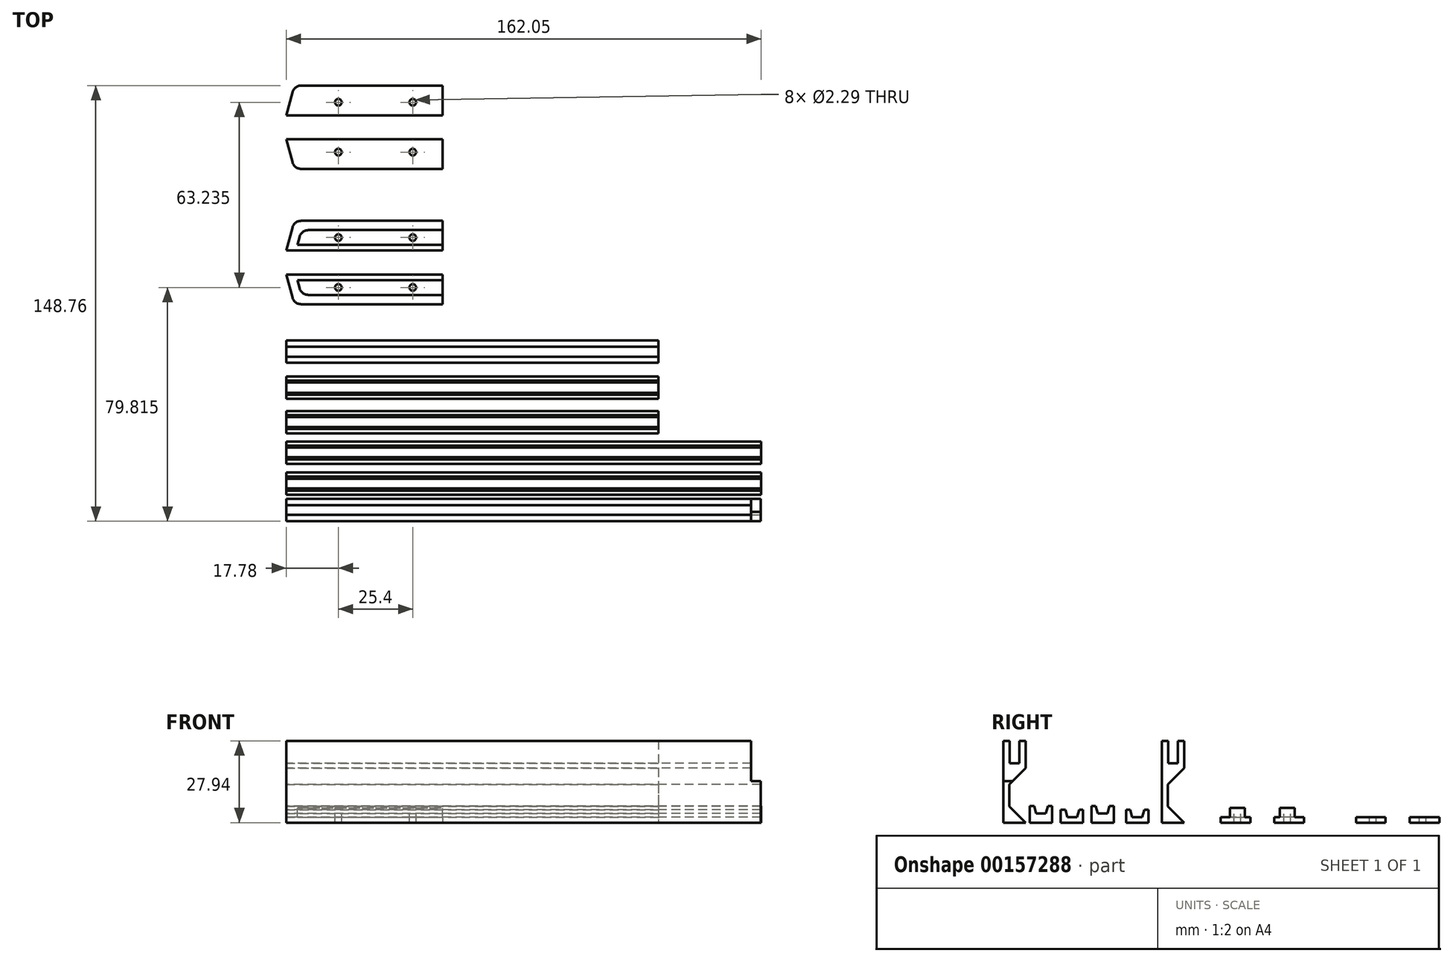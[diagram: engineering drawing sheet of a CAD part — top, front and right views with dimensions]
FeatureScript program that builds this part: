
annotation { "Feature Type Name" : "Feature", "Feature Type Description" : "" }
export const myFeature = defineFeature(function(context is Context, id is Id, definition is map)
    precondition{}
    {
        {
            var Q0;
            Q0=qCreatedBy(makeId("Top.planeOp"),FACE);
            var sketch = newSketch(context, id + "F0", { "sketchPlane" : qUnion([Q0])});
            skLineSegment(sketch, "E0", {"start": v(5.06, 0) * mm, "end": v(53.34, 0) * mm});
            skLineSegment(sketch, "E1", {"start": v(0, 10.16) * mm, "end": v(53.34, 10.16) * mm});
            skLineSegment(sketch, "E2", {"start": v(53.34, 10.16) * mm, "end": v(53.34, 0) * mm});
            skPoint(sketch, "E3.visualSharp", {"position": v(0, 0) * mm});
            skLineSegment(sketch, "E4", {"start": v(0, 14.23) * mm, "end": v(64.91, 14.23) * mm, "construction": true});
            skLineSegment(sketch, "E5", {"start": v(2.12, 2.26) * mm, "end": v(0, 10.16) * mm});
            skPoint(sketch, "E6.visualSharp", {"position": v(2.72, 0) * mm});
            skArc(sketch, "E6.filletArc", {"start": v(2.12, 2.26) * mm, "mid": v(3.2, 0.63) * mm, "end": v(5.06, 0) * mm});
            skLineSegment(sketch, "E7.MirrorCS", {"start": v(0, 18.3) * mm, "end": v(53.34, 18.3) * mm});
            skLineSegment(sketch, "E8.MirrorCS", {"start": v(2.12, 26.2) * mm, "end": v(0, 18.3) * mm});
            skArc(sketch, "E9.MirrorCS", {"start": v(2.12, 26.2) * mm, "mid": v(3.2, 27.83) * mm, "end": v(5.06, 28.46) * mm});
            skLineSegment(sketch, "E10.MirrorCS", {"start": v(5.06, 28.46) * mm, "end": v(53.34, 28.46) * mm});
            skLineSegment(sketch, "E11.MirrorCS", {"start": v(53.34, 18.3) * mm, "end": v(53.34, 28.46) * mm});
            skLineSegment(sketch, "E12", {"start": v(0, 37.33) * mm, "end": v(59.62, 37.33) * mm, "construction": true});
            skLineSegment(sketch, "E13.MirrorCS", {"start": v(5.06, 46.2) * mm, "end": v(53.34, 46.2) * mm});
            skArc(sketch, "E14.MirrorCS", {"start": v(2.12, 48.46) * mm, "mid": v(3.2, 46.83) * mm, "end": v(5.06, 46.2) * mm});
            skLineSegment(sketch, "E15.MirrorCS", {"start": v(2.12, 48.46) * mm, "end": v(0, 56.36) * mm});
            skLineSegment(sketch, "E16.MirrorCS", {"start": v(0, 56.36) * mm, "end": v(53.34, 56.36) * mm});
            skLineSegment(sketch, "E17.MirrorCS", {"start": v(53.34, 56.36) * mm, "end": v(53.34, 46.2) * mm});
            skLineSegment(sketch, "E18.MirrorCS", {"start": v(0, 64.5) * mm, "end": v(53.34, 64.5) * mm});
            skLineSegment(sketch, "E19.MirrorCS", {"start": v(2.12, 72.4) * mm, "end": v(0, 64.5) * mm});
            skArc(sketch, "E20.MirrorCS", {"start": v(2.12, 72.4) * mm, "mid": v(3.2, 74.04) * mm, "end": v(5.06, 74.66) * mm});
            skLineSegment(sketch, "E21.MirrorCS", {"start": v(5.06, 74.66) * mm, "end": v(53.34, 74.66) * mm});
            skLineSegment(sketch, "E22.MirrorCS", {"start": v(53.34, 64.5) * mm, "end": v(53.34, 74.66) * mm});
            skSolve(sketch);
        }
        {
            var Q0;
            Q0 = qSketchRegion(id + "F0", true);
            extrude(context, id + "F1", {"entities" : qUnion([Q0]), "depth" : 1.9 * mm});
        }
        {
            var Q0;
            Q0=makeQuery(id+"F1.opExtrude","CAP_FACE",FACE,{"disambiguationData":[OSD([sQuery(id+"F0.wireOp",EDGE,"E0"),sQuery(id+"F0.wireOp",EDGE,"E1"),sQuery(id+"F0.wireOp",EDGE,"E2"),sQuery(id+"F0.wireOp",EDGE,"5697KqRH-eI2E-rnLH-nUeZ-s4URGK5m77xj"),sQuery(id+"F0.wireOp",EDGE,"92a76409-ad34-472e-83c1-3b65e62bf029.filletArc")])],"isStart":false});
            var sketch = newSketch(context, id + "F2", { "sketchPlane" : qUnion([Q0])});
            skLineSegment(sketch, "E23", {"start": v(53.34, 10.16) * mm, "end": v(3.3, 10.16) * mm});
            skLineSegment(sketch, "E24", {"start": v(7.5, 3.18) * mm, "end": v(53.34, 3.18) * mm});
            skLineSegment(sketch, "E25", {"start": v(4.57, 5.43) * mm, "end": v(3.3, 10.16) * mm});
            skPoint(sketch, "E26.visualSharp", {"position": v(5.17, 3.18) * mm});
            skArc(sketch, "E26.filletArc", {"start": v(4.57, 5.43) * mm, "mid": v(5.65, 3.8) * mm, "end": v(7.5, 3.18) * mm});
            skLineSegment(sketch, "E27", {"start": v(53.34, 10.16) * mm, "end": v(53.34, 3.18) * mm});
            skLineSegment(sketch, "E28.MirrorCS", {"start": v(53.34, 18.3) * mm, "end": v(3.3, 18.3) * mm});
            skLineSegment(sketch, "E29.MirrorCS", {"start": v(4.57, 23.03) * mm, "end": v(3.3, 18.3) * mm});
            skArc(sketch, "E30.MirrorCS", {"start": v(4.57, 23.03) * mm, "mid": v(5.65, 24.66) * mm, "end": v(7.5, 25.29) * mm});
            skLineSegment(sketch, "E31.MirrorCS", {"start": v(7.5, 25.29) * mm, "end": v(53.34, 25.29) * mm});
            skLineSegment(sketch, "E32.MirrorCS", {"start": v(53.34, 18.3) * mm, "end": v(53.34, 25.29) * mm});
            skSolve(sketch);
        }
        {
            var Q0;
            Q0 = qSketchRegion(id + "F2", true);
            extrude(context, id + "F3", {"entities" : qUnion([Q0]), "operationType" : NewBodyOperationType.ADD, "depth" : 3.15 * mm});
        }
        {
            var Q0;
            Q0=makeQuery(id+"F3.boolean.opBoolean","MERGE",FACE,{"derivedFrom":[makeQuery(id+"F1.opExtrude","SWEPT_FACE",FACE,{"disambiguationData":[OSD([sQuery(id+"F0.wireOp",EDGE,"E2")])]}),makeQuery(id+"F3.opExtrude","SWEPT_FACE",FACE,{"disambiguationData":[OSD([sQuery(id+"F2.wireOp",EDGE,"E27")])]})]});
            var sketch = newSketch(context, id + "F4", { "sketchPlane" : qUnion([Q0])});
            skLineSegment(sketch, "E33", {"start": v(10.16, 1.9) * mm, "end": v(8.26, 1.9) * mm});
            skLineSegment(sketch, "E34", {"start": v(8.26, 1.9) * mm, "end": v(8.26, 5.05) * mm});
            skLineSegment(sketch, "E35", {"start": v(8.26, 5.05) * mm, "end": v(10.16, 5.05) * mm});
            skLineSegment(sketch, "E36", {"start": v(10.16, 5.05) * mm, "end": v(10.16, 1.9) * mm});
            skLineSegment(sketch, "E37", {"start": v(14.23, 0) * mm, "end": v(14.23, 7.96) * mm, "construction": true});
            skLineSegment(sketch, "E38.MirrorCS", {"start": v(18.3, 5.05) * mm, "end": v(18.3, 1.9) * mm});
            skLineSegment(sketch, "E39.MirrorCS", {"start": v(20.2, 5.05) * mm, "end": v(18.3, 5.05) * mm});
            skLineSegment(sketch, "E40.MirrorCS", {"start": v(20.2, 1.9) * mm, "end": v(20.2, 5.05) * mm});
            skLineSegment(sketch, "E41.MirrorCS", {"start": v(18.3, 1.9) * mm, "end": v(20.2, 1.9) * mm});
            skSolve(sketch);
        }
        {
            var Q0;
            Q0 = qSketchRegion(id + "F4", true);
            extrude(context, id + "F5", {"entities" : qUnion([Q0]), "operationType" : NewBodyOperationType.REMOVE, "endBound" : BoundingType.UP_TO_NEXT, "oppositeDirection" : true, "depth" : 25.4 * mm});
        }
        {
            var Q0;
            Q0=makeQuery(id+"F3.opExtrude","CAP_FACE",FACE,{"disambiguationData":[OSD([sQuery(id+"F2.wireOp",EDGE,"E23"),sQuery(id+"F2.wireOp",EDGE,"E24"),sQuery(id+"F2.wireOp",EDGE,"E25"),sQuery(id+"F2.wireOp",EDGE,"E26.filletArc"),sQuery(id+"F2.wireOp",EDGE,"E27")])],"isStart":false});
            var sketch = newSketch(context, id + "F6", { "sketchPlane" : qUnion([Q0])});
            skCircle(sketch, "E42", {"center": v(17.78, 5.72) * mm, "radius": 1.14 * mm});
            skCircle(sketch, "E43", {"center": v(43.18, 5.72) * mm, "radius": 1.14 * mm});
            skCircle(sketch, "E44.MirrorC", {"center": v(17.78, 22.75) * mm, "radius": 1.14 * mm});
            skCircle(sketch, "E45.MirrorC", {"center": v(43.18, 22.75) * mm, "radius": 1.14 * mm});
            skCircle(sketch, "E46.MirrorC", {"center": v(17.78, 51.92) * mm, "radius": 1.14 * mm});
            skCircle(sketch, "E47.MirrorC", {"center": v(43.18, 51.92) * mm, "radius": 1.14 * mm});
            skCircle(sketch, "E48.MirrorC", {"center": v(43.18, 68.95) * mm, "radius": 1.14 * mm});
            skCircle(sketch, "E49.MirrorC", {"center": v(17.78, 68.95) * mm, "radius": 1.14 * mm});
            skSolve(sketch);
        }
        {
            var Q0;
            Q0 = qSketchRegion(id + "F6", true);
            extrude(context, id + "F7", {"entities" : qUnion([Q0]), "operationType" : NewBodyOperationType.REMOVE, "endBound" : BoundingType.THROUGH_ALL, "oppositeDirection" : true, "depth" : 25.4 * mm});
        }
        {
            var Q0;
            Q0=qCreatedBy(makeId("Top.planeOp"),FACE);
            var sketch = newSketch(context, id + "F8", { "sketchPlane" : qUnion([Q0])});
            skLineSegment(sketch, "E50.bottom", {"start": v(0, -12.41) * mm, "end": v(127, -12.41) * mm});
            skLineSegment(sketch, "E50.top", {"start": v(0, -20.03) * mm, "end": v(127, -20.03) * mm});
            skLineSegment(sketch, "E50.left", {"start": v(0, -12.41) * mm, "end": v(0, -20.03) * mm});
            skLineSegment(sketch, "E50.right", {"start": v(127, -12.41) * mm, "end": v(127, -20.03) * mm});
            skSolve(sketch);
        }
        {
            var Q0;
            Q0 = qSketchRegion(id + "F8", true);
            extrude(context, id + "F9", {"entities" : qUnion([Q0]), "depth" : 27.94 * mm});
        }
        {
            var Q0;
            Q0=makeQuery(id+"F9.opExtrude","SWEPT_FACE",FACE,{"disambiguationData":[OSD([sQuery(id+"F8.wireOp",EDGE,"E50.right")])]});
            var sketch = newSketch(context, id + "F10", { "sketchPlane" : qUnion([Q0])});
            skLineSegment(sketch, "E51.bottom", {"start": v(-17.9, 27.94) * mm, "end": v(-14.55, 27.94) * mm});
            skLineSegment(sketch, "E51.top", {"start": v(-17.9, 20.32) * mm, "end": v(-14.55, 20.32) * mm});
            skLineSegment(sketch, "E51.left", {"start": v(-17.9, 27.94) * mm, "end": v(-17.9, 20.32) * mm});
            skLineSegment(sketch, "E51.right", {"start": v(-14.55, 27.94) * mm, "end": v(-14.55, 20.32) * mm});
            skLineSegment(sketch, "E52", {"start": v(-12.41, 18.63) * mm, "end": v(-18, 13.05) * mm});
            skLineSegment(sketch, "E53", {"start": v(-18, 13.05) * mm, "end": v(-18, 5.59) * mm});
            skLineSegment(sketch, "E54", {"start": v(-18, 5.59) * mm, "end": v(-12.41, 0) * mm});
            skLineSegment(sketch, "E55", {"start": v(-12.41, 0) * mm, "end": v(-12.41, 18.63) * mm});
            skSolve(sketch);
        }
        {
            var Q0;
            Q0 = qSketchRegion(id + "F10", true);
            extrude(context, id + "F11", {"entities" : qUnion([Q0]), "operationType" : NewBodyOperationType.REMOVE, "endBound" : BoundingType.UP_TO_NEXT, "oppositeDirection" : true, "depth" : 25.4 * mm});
        }
        {
            var Q0;
            Q0=qCreatedBy(makeId("Top.planeOp"),FACE);
            var sketch = newSketch(context, id + "F12", { "sketchPlane" : qUnion([Q0])});
            skLineSegment(sketch, "E56.bottom", {"start": v(0, -24.66) * mm, "end": v(127, -24.66) * mm});
            skLineSegment(sketch, "E56.top", {"start": v(0, -32.28) * mm, "end": v(127, -32.28) * mm});
            skLineSegment(sketch, "E56.left", {"start": v(0, -24.66) * mm, "end": v(0, -32.28) * mm});
            skLineSegment(sketch, "E56.right", {"start": v(127, -24.66) * mm, "end": v(127, -32.28) * mm});
            skSolve(sketch);
        }
        {
            var Q0;
            Q0 = qSketchRegion(id + "F12", true);
            extrude(context, id + "F13", {"entities" : qUnion([Q0]), "depth" : 4.44 * mm});
        }
        {
            var Q0;
            Q0=makeQuery(id+"F13.opExtrude","SWEPT_FACE",FACE,{"disambiguationData":[OSD([sQuery(id+"F12.wireOp",EDGE,"E56.right")])]});
            var sketch = newSketch(context, id + "F14", { "sketchPlane" : qUnion([Q0])});
            skLineSegment(sketch, "E57", {"start": v(-30.88, 4.45) * mm, "end": v(-30.25, 1.9) * mm});
            skLineSegment(sketch, "E58", {"start": v(-30.25, 1.9) * mm, "end": v(-26.7, 1.9) * mm});
            skLineSegment(sketch, "E59", {"start": v(-26.7, 1.9) * mm, "end": v(-26.06, 4.45) * mm});
            skLineSegment(sketch, "E60", {"start": v(-26.06, 4.45) * mm, "end": v(-30.88, 4.45) * mm});
            skSolve(sketch);
        }
        {
            var Q0;
            Q0 = qSketchRegion(id + "F14", true);
            extrude(context, id + "F15", {"entities" : qUnion([Q0]), "operationType" : NewBodyOperationType.REMOVE, "endBound" : BoundingType.UP_TO_NEXT, "oppositeDirection" : true, "depth" : 25.4 * mm});
        }
        {
            var Q0;
            Q0=qCreatedBy(makeId("Top.planeOp"),FACE);
            var sketch = newSketch(context, id + "F16", { "sketchPlane" : qUnion([Q0])});
            skLineSegment(sketch, "E61.bottom", {"start": v(0, -36.46) * mm, "end": v(127, -36.46) * mm});
            skLineSegment(sketch, "E61.top", {"start": v(0, -44.08) * mm, "end": v(127, -44.08) * mm});
            skLineSegment(sketch, "E61.left", {"start": v(0, -36.46) * mm, "end": v(0, -44.08) * mm});
            skLineSegment(sketch, "E61.right", {"start": v(127, -36.46) * mm, "end": v(127, -44.08) * mm});
            skSolve(sketch);
        }
        {
            var Q0;
            Q0 = qSketchRegion(id + "F16", true);
            extrude(context, id + "F17", {"entities" : qUnion([Q0]), "depth" : 5.7 * mm});
        }
        {
            var Q0;
            Q0=makeQuery(id+"F17.opExtrude","SWEPT_FACE",FACE,{"disambiguationData":[OSD([sQuery(id+"F16.wireOp",EDGE,"E61.right")])]});
            var sketch = newSketch(context, id + "F18", { "sketchPlane" : qUnion([Q0])});
            skLineSegment(sketch, "E62", {"start": v(-42.6, 5.72) * mm, "end": v(-41.92, 3.17) * mm});
            skLineSegment(sketch, "E63", {"start": v(-41.92, 3.17) * mm, "end": v(-38.57, 3.18) * mm});
            skLineSegment(sketch, "E64", {"start": v(-38.57, 3.17) * mm, "end": v(-37.9, 5.72) * mm});
            skLineSegment(sketch, "E65", {"start": v(-42.6, 5.72) * mm, "end": v(-37.9, 5.72) * mm});
            skSolve(sketch);
        }
        {
            var Q0;
            Q0 = qSketchRegion(id + "F18", true);
            extrude(context, id + "F19", {"entities" : qUnion([Q0]), "operationType" : NewBodyOperationType.REMOVE, "endBound" : BoundingType.UP_TO_NEXT, "oppositeDirection" : true, "depth" : 25.4 * mm});
        }
        {
            var Q0;
            Q0=qCreatedBy(makeId("Right.planeOp"),FACE);
            var sketch = newSketch(context, id + "F20", { "sketchPlane" : qUnion([Q0])});
            skLineSegment(sketch, "E66", {"start": v(-66.48, 27.94) * mm, "end": v(-66.48, 18.63) * mm});
            skLineSegment(sketch, "E67", {"start": v(-66.48, 0) * mm, "end": v(-74.1, 0) * mm});
            skLineSegment(sketch, "E68", {"start": v(-74.1, 0) * mm, "end": v(-74.1, 27.94) * mm});
            skLineSegment(sketch, "E69", {"start": v(-74.1, 27.94) * mm, "end": v(-71.96, 27.94) * mm});
            skLineSegment(sketch, "E70.top", {"start": v(-71.96, 20.32) * mm, "end": v(-68.6, 20.32) * mm});
            skLineSegment(sketch, "E70.left", {"start": v(-71.96, 27.94) * mm, "end": v(-71.96, 20.32) * mm});
            skLineSegment(sketch, "E70.right", {"start": v(-68.6, 27.94) * mm, "end": v(-68.6, 20.32) * mm});
            skLineSegment(sketch, "E71.trimOffspring", {"start": v(-68.6, 27.94) * mm, "end": v(-66.48, 27.94) * mm});
            skLineSegment(sketch, "E72", {"start": v(-72.06, 5.59) * mm, "end": v(-72.06, 13.05) * mm});
            skLineSegment(sketch, "E73", {"start": v(-72.06, 13.05) * mm, "end": v(-66.48, 18.63) * mm});
            skLineSegment(sketch, "E74", {"start": v(-72.06, 5.59) * mm, "end": v(-66.48, 0) * mm});
            skSolve(sketch);
        }
        {
            var Q0;
            Q0 = qSketchRegion(id + "F20", true);
            extrude(context, id + "F21", {"entities" : qUnion([Q0]), "depth" : 162 * mm});
        }
        {
            var Q0;
            Q0=makeQuery(id+"F21.opExtrude","SWEPT_FACE",FACE,{"disambiguationData":[OSD([sQuery(id+"F20.wireOp",EDGE,"E68")])]});
            var sketch = newSketch(context, id + "F22", { "sketchPlane" : qUnion([Q0])});
            skLineSegment(sketch, "E75.bottom", {"start": v(162, 27.94) * mm, "end": v(158.7, 27.94) * mm});
            skLineSegment(sketch, "E75.top", {"start": v(162, 14.22) * mm, "end": v(158.7, 14.22) * mm});
            skLineSegment(sketch, "E75.left", {"start": v(162, 27.94) * mm, "end": v(162, 14.22) * mm});
            skLineSegment(sketch, "E75.right", {"start": v(158.7, 27.94) * mm, "end": v(158.7, 14.22) * mm});
            skSolve(sketch);
        }
        {
            var Q0;
            Q0 = qSketchRegion(id + "F22", true);
            extrude(context, id + "F23", {"entities" : qUnion([Q0]), "operationType" : NewBodyOperationType.REMOVE, "oppositeDirection" : true, "depth" : 7.62 * mm});
        }
        {
            var Q0;
            Q0=qCreatedBy(makeId("Right.planeOp"),FACE);
            var sketch = newSketch(context, id + "F24", { "sketchPlane" : qUnion([Q0])});
            skLineSegment(sketch, "E76", {"start": v(-46.9, 0) * mm, "end": v(-46.9, 4.44) * mm});
            skLineSegment(sketch, "E77", {"start": v(-46.9, 4.44) * mm, "end": v(-48.25, 4.44) * mm});
            skLineSegment(sketch, "E78", {"start": v(-48.25, 4.45) * mm, "end": v(-48.93, 1.9) * mm});
            skLineSegment(sketch, "E79", {"start": v(-48.93, 1.9) * mm, "end": v(-52.28, 1.9) * mm});
            skLineSegment(sketch, "E80", {"start": v(-52.28, 1.9) * mm, "end": v(-52.96, 4.45) * mm});
            skLineSegment(sketch, "E81", {"start": v(-52.96, 4.44) * mm, "end": v(-54.52, 4.44) * mm});
            skLineSegment(sketch, "E82", {"start": v(-54.52, 4.44) * mm, "end": v(-54.52, 0) * mm});
            skLineSegment(sketch, "E83", {"start": v(-54.52, 0) * mm, "end": v(-46.9, 0) * mm});
            skLineSegment(sketch, "E84", {"start": v(-57.46, 0) * mm, "end": v(-57.46, 5.71) * mm});
            skLineSegment(sketch, "E85", {"start": v(-57.46, 5.71) * mm, "end": v(-58.9, 5.71) * mm});
            skLineSegment(sketch, "E86", {"start": v(-58.9, 5.71) * mm, "end": v(-59.59, 3.17) * mm});
            skLineSegment(sketch, "E87", {"start": v(-59.59, 3.17) * mm, "end": v(-62.94, 3.17) * mm});
            skLineSegment(sketch, "E88", {"start": v(-62.94, 3.17) * mm, "end": v(-63.62, 5.71) * mm});
            skLineSegment(sketch, "E89", {"start": v(-63.62, 5.71) * mm, "end": v(-65.08, 5.71) * mm});
            skLineSegment(sketch, "E90", {"start": v(-65.08, 5.71) * mm, "end": v(-65.08, 0) * mm});
            skLineSegment(sketch, "E91", {"start": v(-65.08, 0) * mm, "end": v(-57.46, 0) * mm});
            skSolve(sketch);
        }
        {
            var Q0;
            Q0 = qSketchRegion(id + "F24", true);
            extrude(context, id + "F25", {"entities" : qUnion([Q0]), "depth" : 162.05 * mm});
        }
    });
